# Revit family: VENTS-VKV_EC
name_source: partatom
category: Mechanical Equipment
units: mm (PartAtom-declared; Revit-internal decimal feet)

## family parameters
Always vertical = Yes
Classification = None
Cut with Voids When Loaded = No
OmniClass Number = 23.75.35.17.14
OmniClass Title = Fans, Single Units
Part Type = Normal
Room Calculation Point = No
Round Connector Dimension = Use Diameter
Shared = No
Work Plane-Based = No

## types (11) — shared parameters
Casing Material = Fan Zinc
DboxFixDepth = 2 mm  [stored 0.00656168 ft]
DboxFixW = 80 mm  [stored 0.262467 ft]
Description = Centrifugal roof fan with vertical air discharge
Family Version = 1.0
Grid Material = Cover Grid Cross
Load Classification = HVAC
Maintenance Zone Front Depth = 400 mm
Maintenance Zone Material = Maintenance Zone
Maintenance Zone Side Depth = 400 mm
Manufacturer = Vents
Power Factor = 1
Protection rating = IP X4
URL = https://ventilation-system.com
zero-valued in all types: Sound Pressure Level at 1 m (dBA), Sound Pressure Level at 3 m (dBA)

## per-type parameters (varying)
| type | A | Af | AswBottom | Current | D | DboxFixBottomH | DboxFixH | Duct Connection Size | H | Hb | Hc | Ht | L | L2 | Maximum Air Flow | Noise Level at 3 m (dBa) | Number of Poles | RPM (min-1) | Transported Air Temperature (°C) | Type Comments | Voltage | Weight | gsA |
| VKV 190 EC | 417 mm | 155 mm | 320 mm | 1 A | 213 mm  [stored 0.698819 ft] | 40 mm  [stored 0.131234 ft] | 112 mm  [stored 0.367454 ft] | 180 mm  [stored 0.590551 ft] | 166 mm  [stored 0.544619 ft] | 36 mm  [stored 0.11811 ft] | 78 mm | 52 mm  [stored 0.170604 ft] | 355 mm | 470 mm | 670 m³/h | 52 | 1 | 3520 | -25...+60 | Centrifugal roof fan VKV 190 EC | 230 V | 7.00 kg | 334 mm |
| VKV 225 EC | 417 mm | 155 mm | 320 mm | 1 A | 213 mm  [stored 0.698819 ft] | 40 mm  [stored 0.131234 ft] | 122 mm  [stored 0.400262 ft] | 180 mm  [stored 0.590551 ft] | 210 mm  [stored 0.688976 ft] | 31 mm  [stored 0.101706 ft] | 131 mm  [stored 0.42979 ft] | 48 mm  [stored 0.15748 ft] | 355 mm | 470 mm | 1290 m³/h | 47 | 1 | 2400 | -25...+60 | Centrifugal roof fan VKV 225 EC | 230 V | 7.00 kg | 334 mm |
| VKV 250 EC | 481 mm | 179 mm | 358 mm | 1 A | 285 mm | 36 mm  [stored 0.11811 ft] | 151 mm  [stored 0.495407 ft] | 250 mm  [stored 0.82021 ft] | 236 mm | 31 mm  [stored 0.101706 ft] | 154 mm  [stored 0.505249 ft] | 51 mm  [stored 0.167323 ft] | 425 mm | 534 mm | 1470 m³/h | 54 | 1 | 3300 | -25...+60 | Centrifugal roof fan VKV 250 EC | 230 V | 11.00 kg | 385 mm |
| VKV 280 EC | 547 mm | 204 mm | 395 mm | 1 A | 285 mm | 53 mm  [stored 0.173885 ft] | 151 mm  [stored 0.495407 ft] | 250 mm  [stored 0.82021 ft] | 274 mm  [stored 0.89895 ft] | 31 mm  [stored 0.101706 ft] | 192 mm  [stored 0.629921 ft] | 51 mm  [stored 0.167323 ft] | 425 mm | 600 mm | 2330 m³/h | 48 | 1 | 2610 | -20...+60 | Centrifugal roof fan VKV 280 EC | 230 V | 14.00 kg | 438 mm |
| VKV 310 EC | 613 mm | 229 mm | 445 mm | 2 A | 285 mm | 75 mm | 151 mm  [stored 0.495407 ft] | 250 mm  [stored 0.82021 ft] | 296 mm | 31 mm  [stored 0.101706 ft] | 214 mm  [stored 0.7021 ft] | 51 mm  [stored 0.167323 ft] | 477 mm | 666 mm | 3100 m³/h | 49 | 1 | 2600 | -20...+60 | Centrifugal roof fan VKV 310 EC | 230 V | 20.00 kg | 490 mm |
| VKV 355 EC | 738 mm | 275 mm | 546 mm | 9 A | 438 mm | 105 mm  [stored 0.344488 ft] | 151 mm  [stored 0.495407 ft] | 400 mm | 326 mm | 31 mm  [stored 0.101706 ft] | 244 mm  [stored 0.800525 ft] | 51 mm  [stored 0.167323 ft] | 598 mm | 791 mm | 3830 m³/h | 51 | 1 | 1550 | -25...+50 | Centrifugal roof fan VKV 355 EC | 230 V | 23.00 kg | 590 mm |
| VKV 400 EC | 738 mm | 275 mm | 562 mm | 4 A | 438 mm | 82 mm  [stored 0.269029 ft] | 151 mm  [stored 0.495407 ft] | 400 mm | 371 mm | 31 mm  [stored 0.101706 ft] | 220 mm  [stored 0.721785 ft] | 120 mm  [stored 0.393701 ft] | 598 mm | 791 mm | 5380 m³/h | 58 | 1 | 1450 | -25...+50 | Centrifugal roof fan VKV 400 EC | 230 V | 25.00 kg | 590 mm |
| VKV 450 EC | 738 mm | 275 mm | 546 mm | 3 A | 438 mm | 124 mm  [stored 0.406824 ft] | 151 mm  [stored 0.495407 ft] | 400 mm | 425 mm | 31 mm  [stored 0.101706 ft] | 304 mm | 90 mm  [stored 0.295276 ft] | 668 mm | 791 mm | 8110 m³/h | 63 | 3 | 1560 | -20...+60 | Centrifugal roof fan VKV 450 EC | 400 V | 44.00 kg | 590 mm |
| VKV 500 EC | 859 mm | 320 mm | 594 mm | 2 A | 438 mm | 198 mm  [stored 0.649606 ft] | 151 mm  [stored 0.495407 ft] | 400 mm | 456 mm | 31 mm  [stored 0.101706 ft] | 335 mm | 90 mm  [stored 0.295276 ft] | 668 mm | 912 mm | 10900 m³/h | 67 | 3 | 1480 | -25...+50 | Centrifugal roof fan VKV 500 EC | 400 V | 52.00 kg | 687 mm |
| VKV 560 EC | 859 mm | 320 mm | 722 mm | 4 A | 605 mm | 150 mm | 151 mm  [stored 0.495407 ft] | 560 mm | 478 mm | 31 mm  [stored 0.101706 ft] | 335 mm | 112 mm  [stored 0.367454 ft] | 850 mm | 912 mm | 13640 m³/h | 69 | 3 | 1540 | -25...+60 | Centrifugal roof fan VKV 560 EC | 400 V | 65.00 kg | 687 mm |
| VKV 630 EC | 951 mm | 355 mm | 782 mm | 5 A | 605 mm | 186 mm  [stored 0.610236 ft] | 151 mm  [stored 0.495407 ft] | 560 mm | 530 mm | 36 mm  [stored 0.11811 ft] | 382 mm | 112 mm  [stored 0.367454 ft] | 939 mm | 1004 mm | 18270 m³/h | 71 | 3 | 1450 | -25...+55 | Centrifugal roof fan VKV 630 EC | 400 V | 83.00 kg | 761 mm |

note: column(s) folded — value = type name in every type: Model

note: [stored X ft] marks values corroborated as IEEE doubles in the binary element streams (Revit-internal decimal feet)

## geometry (parser evidence)
native form markers: Sweep x9
no freeform markers — native parametric forms only
